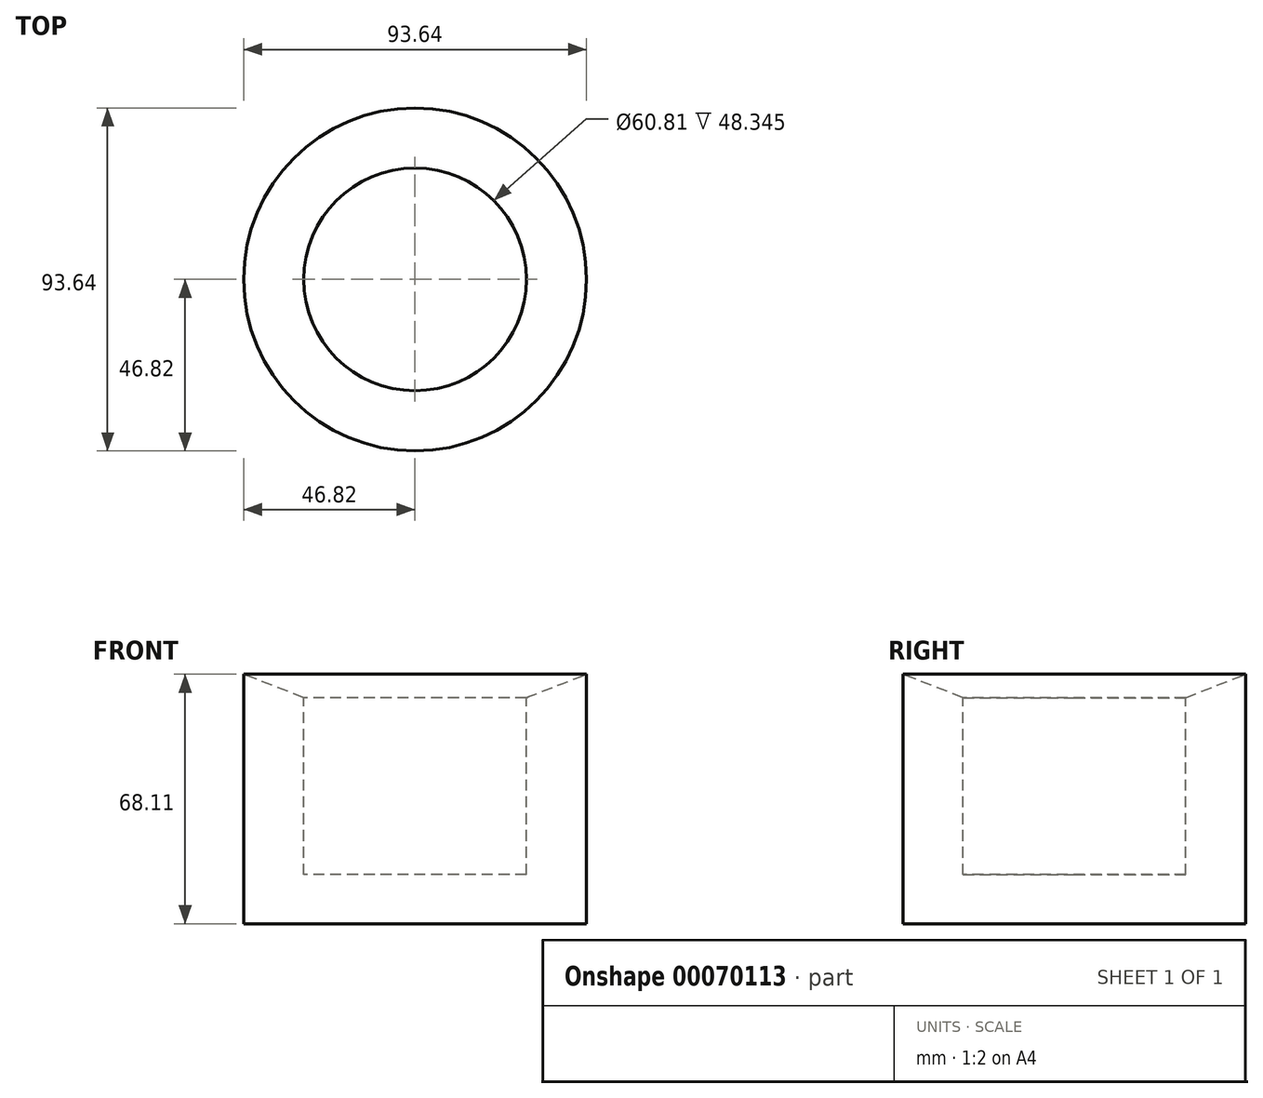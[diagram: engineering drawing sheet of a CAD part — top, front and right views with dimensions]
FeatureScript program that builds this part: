
annotation { "Feature Type Name" : "Feature", "Feature Type Description" : "" }
export const myFeature = defineFeature(function(context is Context, id is Id, definition is map)
    precondition{}
    {
        {
            var Q0;
            Q0=qCreatedBy(makeId("Front.planeOp"),FACE);
            var sketch = newSketch(context, id + "F0", { "sketchPlane" : qUnion([Q0])});
            skLineSegment(sketch, "E0", {"start": v(0, 0) * mm, "end": v(-46.82, 0) * mm});
            skLineSegment(sketch, "E1", {"start": v(-46.82, 0) * mm, "end": v(-46.82, 68.1) * mm});
            skLineSegment(sketch, "E2", {"start": v(-46.82, 68.1) * mm, "end": v(-30.4, 61.72) * mm});
            skLineSegment(sketch, "E3", {"start": v(-30.4, 61.72) * mm, "end": v(-30.4, 13.38) * mm});
            skLineSegment(sketch, "E4", {"start": v(-30.4, 13.38) * mm, "end": v(0, 13.38) * mm});
            skLineSegment(sketch, "E5", {"start": v(0, 13.38) * mm, "end": v(0, 0) * mm});
            skSolve(sketch);
        }
        {
            var Q0;
            Q0=makeQuery(id+"F0.imprint","IMPRINT",FACE,{"disambiguationData":[TD([[makeQuery(id+"F0.imprint","IMPRINT",EDGE,{"derivedFrom":sQuery(id+"F0.wireOp",EDGE,"E0")}),-1.0]])]});
            var Q1;
            Q1=sQuery(id+"F0.wireOp",EDGE,"E5");
            revolve(context, id + "F1", {"entities" : qUnion([Q0]), "axis" : qUnion([Q1]), "revolveType" : RevolveType.FULL});
        }
    });
